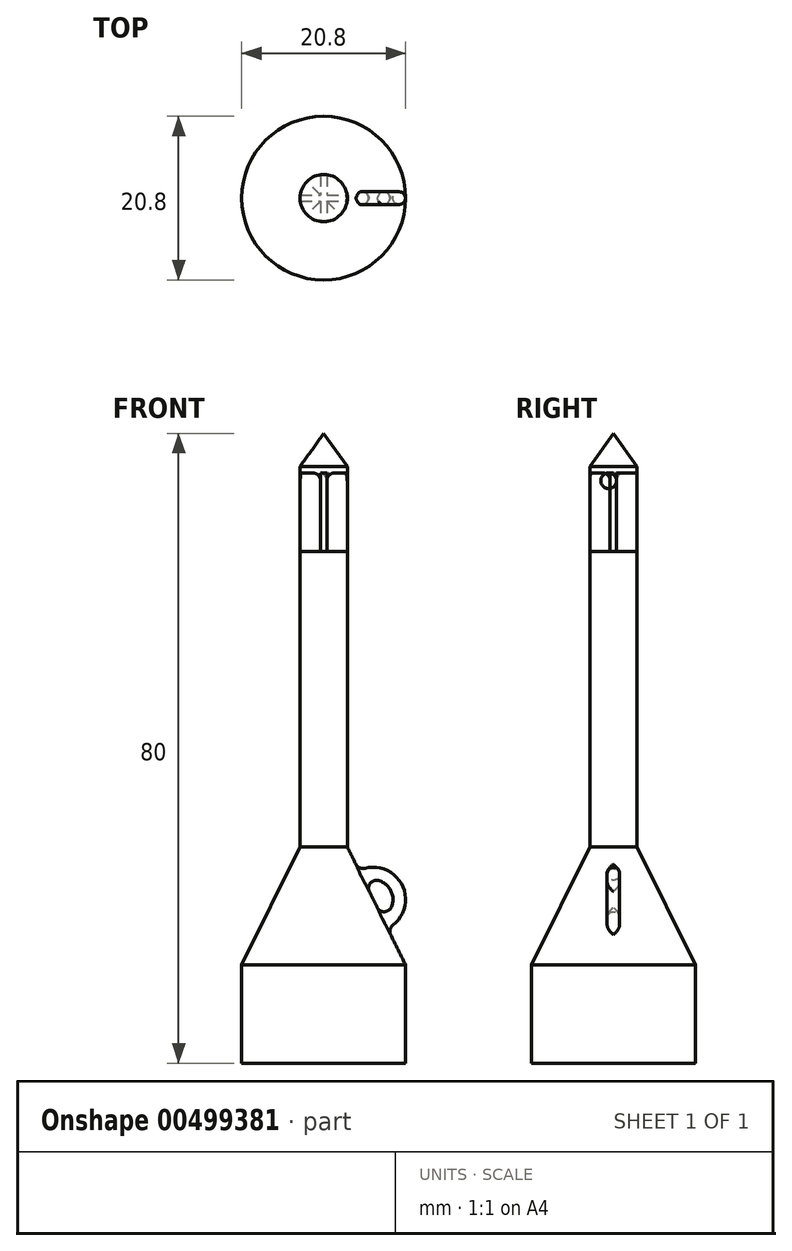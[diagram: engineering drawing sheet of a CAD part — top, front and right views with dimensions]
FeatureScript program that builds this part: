
annotation { "Feature Type Name" : "Feature", "Feature Type Description" : "" }
export const myFeature = defineFeature(function(context is Context, id is Id, definition is map)
    precondition{}
    {
        {
            var Q0;
            Q0=qCreatedBy(makeId("Front.planeOp"),FACE);
            var sketch = newSketch(context, id + "F0", { "sketchPlane" : qUnion([Q0])});
            skLineSegment(sketch, "E0", {"start": v(0, 0) * mm, "end": v(10.4, 0) * mm});
            skLineSegment(sketch, "E1", {"start": v(10.4, 0) * mm, "end": v(10.4, 12.5) * mm});
            skLineSegment(sketch, "E2", {"start": v(10.4, 12.5) * mm, "end": v(3, 27.5) * mm});
            skLineSegment(sketch, "E3", {"start": v(3, 27.5) * mm, "end": v(3, 65) * mm});
            skLineSegment(sketch, "E4", {"start": v(3, 65) * mm, "end": v(0, 65) * mm});
            skLineSegment(sketch, "E5", {"start": v(0, 65) * mm, "end": v(0, 0) * mm});
            skLineSegment(sketch, "E6", {"start": v(0, 53.14) * mm, "end": v(0, -5.64) * mm, "construction": true});
            skSolve(sketch);
        }
        {
            var Q0;
            Q0=makeQuery(id+"F0.imprint","IMPRINT",FACE,{"disambiguationData":[TD([[makeQuery(id+"F0.imprint","IMPRINT",EDGE,{"derivedFrom":sQuery(id+"F0.wireOp",EDGE,"E0")}),1.0]])]});
            var Q1;
            Q1=qConstructionFilter(qBodyType(qCreatedBy(id+"F0",EDGE),BodyType.WIRE),ConstructionObject.NO);
            var Q2;
            Q2=sQuery(id+"F0.wireOp",EDGE,"E6");
            revolve(context, id + "F1", {"entities" : qUnion([Q0]), "surfaceEntities" : qUnion([Q1]), "axis" : qUnion([Q2]), "revolveType" : RevolveType.FULL});
        }
        {
            var Q0;
            Q0=qCreatedBy(makeId("Front.planeOp"),FACE);
            var sketch = newSketch(context, id + "F2", { "sketchPlane" : qUnion([Q0])});
            skArc(sketch, "E7", {"start": v(6.96, 16.75) * mm, "mid": v(9.98, 22.61) * mm, "end": v(3.5, 23.79) * mm});
            skArc(sketch, "E8", {"start": v(6.2, 18.3) * mm, "mid": v(8.54, 21.9) * mm, "end": v(4.26, 22.24) * mm});
            skLineSegment(sketch, "E9", {"start": v(-9.82, 13.68) * mm, "end": v(-0.94, 31.69) * mm, "construction": true});
            skLineSegment(sketch, "E10", {"start": v(0.94, 31.69) * mm, "end": v(9.82, 13.68) * mm, "construction": true});
            skLineSegment(sketch, "E11", {"start": v(3.5, 23.79) * mm, "end": v(4.26, 22.24) * mm});
            skLineSegment(sketch, "E12.trimOffspring", {"start": v(6.2, 18.3) * mm, "end": v(6.96, 16.75) * mm});
            skLineSegment(sketch, "E13", {"start": v(0, 43.75) * mm, "end": v(0, 5.8) * mm, "construction": true});
            skArc(sketch, "E14.MirrorCS", {"start": v(-6.96, 16.75) * mm, "mid": v(-9.98, 22.61) * mm, "end": v(-3.5, 23.79) * mm});
            skArc(sketch, "E15.MirrorCS", {"start": v(-6.2, 18.3) * mm, "mid": v(-8.54, 21.9) * mm, "end": v(-4.26, 22.24) * mm});
            skLineSegment(sketch, "E16.MirrorCS", {"start": v(-6.2, 18.3) * mm, "end": v(-6.96, 16.75) * mm});
            skLineSegment(sketch, "E17.MirrorCS", {"start": v(-3.5, 23.79) * mm, "end": v(-4.26, 22.24) * mm});
            skSolve(sketch);
        }
        {
            var Q0;
            Q0=makeQuery(id+"F2.imprint","IMPRINT",FACE,{"disambiguationData":[TD([[makeQuery(id+"F2.imprint","IMPRINT",EDGE,{"derivedFrom":sQuery(id+"F2.wireOp",EDGE,"E14.MirrorCS")}),-1.0]])]});
            var Q1;
            Q1=makeQuery(id+"F2.imprint","IMPRINT",FACE,{"disambiguationData":[TD([[makeQuery(id+"F2.imprint","IMPRINT",EDGE,{"derivedFrom":sQuery(id+"F2.wireOp",EDGE,"E7")}),1.0]])]});
            extrude(context, id + "F3", {"entities" : qUnion([Q0, Q1]), "operationType" : NewBodyOperationType.ADD, "endBound" : BoundingType.SYMMETRIC, "depth" : 1.6 * mm});
        }
        {
            var Q0;
            Q0=makeQuery(id+"F1.opRevolve","SWEPT_FACE",FACE,{"disambiguationData":[OSD([sQuery(id+"F0.wireOp",EDGE,"E4")])]});
            var sketch = newSketch(context, id + "F4", { "sketchPlane" : qUnion([Q0])});
            skLineSegment(sketch, "E18.bottom", {"start": v(-0.4, 3) * mm, "end": v(0.4, 3) * mm});
            skLineSegment(sketch, "E18.top", {"start": v(-0.4, -3) * mm, "end": v(0.4, -3) * mm});
            skLineSegment(sketch, "E18.left", {"start": v(-0.4, 3) * mm, "end": v(-0.4, 0.4) * mm});
            skLineSegment(sketch, "E18.right", {"start": v(0.4, 3) * mm, "end": v(0.4, 0.4) * mm});
            skLineSegment(sketch, "E19.bottom", {"start": v(-3, 0.4) * mm, "end": v(-0.4, 0.4) * mm});
            skLineSegment(sketch, "E19.top", {"start": v(-3, -0.4) * mm, "end": v(-0.4, -0.4) * mm});
            skLineSegment(sketch, "E19.left", {"start": v(-3, 0.4) * mm, "end": v(-3, -0.4) * mm});
            skLineSegment(sketch, "E19.right", {"start": v(3, 0.4) * mm, "end": v(3, -0.4) * mm});
            skLineSegment(sketch, "E20", {"start": v(0, 2.58) * mm, "end": v(0, -2.8) * mm, "construction": true});
            skLineSegment(sketch, "E21", {"start": v(-2.51, 0) * mm, "end": v(2.57, 0) * mm, "construction": true});
            skLineSegment(sketch, "E22.trimOffspring", {"start": v(0.4, 0.4) * mm, "end": v(3, 0.4) * mm});
            skLineSegment(sketch, "E23.trimOffspring", {"start": v(0.4, -0.4) * mm, "end": v(0.4, -3) * mm});
            skLineSegment(sketch, "E24.trimOffspring", {"start": v(0.4, -0.4) * mm, "end": v(3, -0.4) * mm});
            skLineSegment(sketch, "E25.trimOffspring", {"start": v(-0.4, -0.4) * mm, "end": v(-0.4, -3) * mm});
            skSolve(sketch);
        }
        {
            var Q0;
            Q0=qSketchRegion(id+"F4",true);
            extrude(context, id + "F5", {"entities" : qUnion([Q0]), "operationType" : NewBodyOperationType.ADD, "depth" : 10 * mm});
        }
        {
            var Q0;
            Q0=qCreatedBy(makeId("Front.planeOp"),FACE);
            var sketch = newSketch(context, id + "F6", { "sketchPlane" : qUnion([Q0])});
            skLineSegment(sketch, "E26.0.0", {"start": v(0.4, 65) * mm, "end": v(2.97, 65) * mm, "construction": true});
            skLineSegment(sketch, "E26.0.1", {"start": v(2.97, 65) * mm, "end": v(3, 65) * mm, "construction": true});
            skLineSegment(sketch, "E26.0.2", {"start": v(3, 65) * mm, "end": v(3, 75) * mm, "construction": true});
            skLineSegment(sketch, "E26.0.4", {"start": v(0.4, 75) * mm, "end": v(0.4, 65) * mm, "construction": true});
            skLineSegment(sketch, "E27", {"start": v(0, 83.64) * mm, "end": v(0, 72.25) * mm, "construction": true});
            skLineSegment(sketch, "E28", {"start": v(3, 75) * mm, "end": v(3, 75.8) * mm});
            skLineSegment(sketch, "E29", {"start": v(3, 75.8) * mm, "end": v(0, 80) * mm});
            skLineSegment(sketch, "E30", {"start": v(0, 80) * mm, "end": v(0, 75) * mm});
            skLineSegment(sketch, "E31", {"start": v(0, 75) * mm, "end": v(3, 75) * mm});
            skSolve(sketch);
        }
        {
            var Q0;
            Q0=makeQuery(id+"F6.imprint","IMPRINT",FACE,{"disambiguationData":[TD([[makeQuery(id+"F6.imprint","IMPRINT",EDGE,{"derivedFrom":sQuery(id+"F6.wireOp",EDGE,"sfQvweTP-yfMo-TDxM-7ycy-mknhdcVdmoTF")}),1.0]])]});
            var Q1;
            Q1=makeQuery(id+"F6.imprint","IMPRINT",FACE,{"disambiguationData":[TD([[makeQuery(id+"F6.imprint","IMPRINT",EDGE,{"derivedFrom":sQuery(id+"F6.wireOp",EDGE,"E28")}),1.0]])]});
            var Q2;
            Q2=sQuery(id+"F6.wireOp",EDGE,"E27");
            revolve(context, id + "F7", {"operationType" : NewBodyOperationType.ADD, "entities" : qUnion([Q0, Q1]), "axis" : qUnion([Q2]), "revolveType" : RevolveType.FULL});
        }
        {
            var Q0;
            Q0=makeQuery(id+"F3.boolean.opBoolean","INTERSECT",EDGE,{"disambiguationData":[OD(0.0)],"derivedFrom":[makeQuery(id+"F1.opRevolve","SWEPT_FACE",FACE,{"disambiguationData":[OSD([sQuery(id+"F0.wireOp",EDGE,"E2")])]}),makeQuery(id+"F3.opExtrude","SWEPT_FACE",FACE,{"disambiguationData":[OSD([sQuery(id+"F2.wireOp",EDGE,"E7")])]})]});
            var Q1;
            Q1=makeQuery(id+"F3.boolean.opBoolean","INTERSECT",EDGE,{"disambiguationData":[OD(1.0)],"derivedFrom":[makeQuery(id+"F1.opRevolve","SWEPT_FACE",FACE,{"disambiguationData":[OSD([sQuery(id+"F0.wireOp",EDGE,"E2")])]}),makeQuery(id+"F3.opExtrude","SWEPT_FACE",FACE,{"disambiguationData":[OSD([sQuery(id+"F2.wireOp",EDGE,"E14.MirrorCS")])]})]});
            var Q2;
            Q2=makeQuery(id+"F3.boolean.opBoolean","INTERSECT",EDGE,{"disambiguationData":[OD(0.0)],"derivedFrom":[makeQuery(id+"F1.opRevolve","SWEPT_FACE",FACE,{"disambiguationData":[OSD([sQuery(id+"F0.wireOp",EDGE,"E2")])]}),makeQuery(id+"F3.opExtrude","SWEPT_FACE",FACE,{"disambiguationData":[OSD([sQuery(id+"F2.wireOp",EDGE,"E15.MirrorCS")])]})]});
            var Q3;
            Q3=makeQuery(id+"F3.boolean.opBoolean","INTERSECT",EDGE,{"disambiguationData":[OD(1.0)],"derivedFrom":[makeQuery(id+"F1.opRevolve","SWEPT_FACE",FACE,{"disambiguationData":[OSD([sQuery(id+"F0.wireOp",EDGE,"E2")])]}),makeQuery(id+"F3.opExtrude","SWEPT_FACE",FACE,{"disambiguationData":[OSD([sQuery(id+"F2.wireOp",EDGE,"E8")])]})]});
            var Q4;
            Q4=makeQuery(id+"F3.boolean.opBoolean","INTERSECT",EDGE,{"disambiguationData":[OD(1.0)],"derivedFrom":[makeQuery(id+"F1.opRevolve","SWEPT_FACE",FACE,{"disambiguationData":[OSD([sQuery(id+"F0.wireOp",EDGE,"E2")])]}),makeQuery(id+"F3.opExtrude","SWEPT_FACE",FACE,{"disambiguationData":[OSD([sQuery(id+"F2.wireOp",EDGE,"E7")])]})]});
            var Q5;
            Q5=makeQuery(id+"F3.boolean.opBoolean","INTERSECT",EDGE,{"disambiguationData":[OD(0.0)],"derivedFrom":[makeQuery(id+"F1.opRevolve","SWEPT_FACE",FACE,{"disambiguationData":[OSD([sQuery(id+"F0.wireOp",EDGE,"E2")])]}),makeQuery(id+"F3.opExtrude","SWEPT_FACE",FACE,{"disambiguationData":[OSD([sQuery(id+"F2.wireOp",EDGE,"E14.MirrorCS")])]})]});
            var Q6;
            Q6=makeQuery(id+"F3.boolean.opBoolean","INTERSECT",EDGE,{"disambiguationData":[OD(1.0)],"derivedFrom":[makeQuery(id+"F1.opRevolve","SWEPT_FACE",FACE,{"disambiguationData":[OSD([sQuery(id+"F0.wireOp",EDGE,"E2")])]}),makeQuery(id+"F3.opExtrude","SWEPT_FACE",FACE,{"disambiguationData":[OSD([sQuery(id+"F2.wireOp",EDGE,"E15.MirrorCS")])]})]});
            var Q7;
            Q7=makeQuery(id+"F3.boolean.opBoolean","INTERSECT",EDGE,{"disambiguationData":[OD(0.0)],"derivedFrom":[makeQuery(id+"F1.opRevolve","SWEPT_FACE",FACE,{"disambiguationData":[OSD([sQuery(id+"F0.wireOp",EDGE,"E2")])]}),makeQuery(id+"F3.opExtrude","SWEPT_FACE",FACE,{"disambiguationData":[OSD([sQuery(id+"F2.wireOp",EDGE,"E8")])]})]});
            fillet(context, id + "F8", {"entities" : qUnion([Q0, Q1, Q2, Q3, Q4, Q5, Q6, Q7]), "radius" : 1 * mm, "tangentPropagation" : true, "allowEdgeOverflow" : false});
        }
        {
            var Q0;
            {var subQ0=sQuery(id+"F4.wireOp",EDGE,"E19.top");Q0=makeQuery(id+"F7.boolean.opBoolean","SPLIT",EDGE,{"disambiguationData":[topologyDisambiguationEdgeConnected([makeQuery(id+"F7.opRevolve","SWEPT_FACE",FACE,{"disambiguationData":[OSD([sQuery(id+"F6.wireOp",EDGE,"E31")])]})])],"derivedFrom":makeQuery(id+"F5.opExtrude","CAP_EDGE",EDGE,{"disambiguationData":[OSD([subQ0])],"isStart":false})});}
            var Q1;
            {var subQ0=sQuery(id+"F4.wireOp",EDGE,"E24.trimOffspring");Q1=makeQuery(id+"F7.boolean.opBoolean","SPLIT",EDGE,{"disambiguationData":[topologyDisambiguationEdgeConnected([makeQuery(id+"F7.opRevolve","SWEPT_FACE",FACE,{"disambiguationData":[OSD([sQuery(id+"F6.wireOp",EDGE,"E31")])]})])],"derivedFrom":makeQuery(id+"F5.opExtrude","CAP_EDGE",EDGE,{"disambiguationData":[OSD([subQ0])],"isStart":false})});}
            var Q2;
            {var subQ0=sQuery(id+"F4.wireOp",EDGE,"E25.trimOffspring");Q2=makeQuery(id+"F7.boolean.opBoolean","SPLIT",EDGE,{"disambiguationData":[topologyDisambiguationEdgeConnected([makeQuery(id+"F7.opRevolve","SWEPT_FACE",FACE,{"disambiguationData":[OSD([sQuery(id+"F6.wireOp",EDGE,"E31")])]})])],"derivedFrom":makeQuery(id+"F5.opExtrude","CAP_EDGE",EDGE,{"disambiguationData":[OSD([subQ0])],"isStart":false})});}
            var Q3;
            {var subQ0=sQuery(id+"F4.wireOp",EDGE,"E22.trimOffspring");Q3=makeQuery(id+"F7.boolean.opBoolean","SPLIT",EDGE,{"disambiguationData":[topologyDisambiguationEdgeConnected([makeQuery(id+"F7.opRevolve","SWEPT_FACE",FACE,{"disambiguationData":[OSD([sQuery(id+"F6.wireOp",EDGE,"E31")])]})])],"derivedFrom":makeQuery(id+"F5.opExtrude","CAP_EDGE",EDGE,{"disambiguationData":[OSD([subQ0])],"isStart":false})});}
            var Q4;
            {var subQ0=sQuery(id+"F4.wireOp",EDGE,"E19.bottom");Q4=makeQuery(id+"F7.boolean.opBoolean","SPLIT",EDGE,{"disambiguationData":[topologyDisambiguationEdgeConnected([makeQuery(id+"F7.opRevolve","SWEPT_FACE",FACE,{"disambiguationData":[OSD([sQuery(id+"F6.wireOp",EDGE,"E31")])]})])],"derivedFrom":makeQuery(id+"F5.opExtrude","CAP_EDGE",EDGE,{"disambiguationData":[OSD([subQ0])],"isStart":false})});}
            var Q5;
            {var subQ0=sQuery(id+"F4.wireOp",EDGE,"E18.right");Q5=makeQuery(id+"F7.boolean.opBoolean","SPLIT",EDGE,{"disambiguationData":[topologyDisambiguationEdgeConnected([makeQuery(id+"F7.opRevolve","SWEPT_FACE",FACE,{"disambiguationData":[OSD([sQuery(id+"F6.wireOp",EDGE,"E31")])]})])],"derivedFrom":makeQuery(id+"F5.opExtrude","CAP_EDGE",EDGE,{"disambiguationData":[OSD([subQ0])],"isStart":false})});}
            var Q6;
            {var subQ0=sQuery(id+"F4.wireOp",EDGE,"E23.trimOffspring");Q6=makeQuery(id+"F7.boolean.opBoolean","SPLIT",EDGE,{"disambiguationData":[topologyDisambiguationEdgeConnected([makeQuery(id+"F7.opRevolve","SWEPT_FACE",FACE,{"disambiguationData":[OSD([sQuery(id+"F6.wireOp",EDGE,"E31")])]})])],"derivedFrom":makeQuery(id+"F5.opExtrude","CAP_EDGE",EDGE,{"disambiguationData":[OSD([subQ0])],"isStart":false})});}
            var Q7;
            {var subQ0=sQuery(id+"F4.wireOp",EDGE,"E18.left");Q7=makeQuery(id+"F7.boolean.opBoolean","SPLIT",EDGE,{"disambiguationData":[topologyDisambiguationEdgeConnected([makeQuery(id+"F7.opRevolve","SWEPT_FACE",FACE,{"disambiguationData":[OSD([sQuery(id+"F6.wireOp",EDGE,"E31")])]})])],"derivedFrom":makeQuery(id+"F5.opExtrude","CAP_EDGE",EDGE,{"disambiguationData":[OSD([subQ0])],"isStart":false})});}
            fillet(context, id + "F9", {"entities" : qUnion([Q0, Q1, Q2, Q3, Q4, Q5, Q6, Q7]), "radius" : 1 * mm, "tangentPropagation" : true, "allowEdgeOverflow" : false});
        }
        {
            var Q0;
            Q0=makeQuery(id+"F3.opExtrude","CAP_EDGE",EDGE,{"disambiguationData":[OSD([sQuery(id+"F2.wireOp",EDGE,"E14.MirrorCS")])],"isStart":true});
            var Q1;
            Q1=makeQuery(id+"F3.opExtrude","CAP_EDGE",EDGE,{"disambiguationData":[OSD([sQuery(id+"F2.wireOp",EDGE,"E14.MirrorCS")])],"isStart":false});
            var Q2;
            Q2=makeQuery(id+"F3.opExtrude","CAP_EDGE",EDGE,{"disambiguationData":[OSD([sQuery(id+"F2.wireOp",EDGE,"E15.MirrorCS")])],"isStart":true});
            var Q3;
            Q3=makeQuery(id+"F3.opExtrude","CAP_EDGE",EDGE,{"disambiguationData":[OSD([sQuery(id+"F2.wireOp",EDGE,"E15.MirrorCS")])],"isStart":false});
            var Q4;
            Q4=makeQuery(id+"F3.opExtrude","CAP_EDGE",EDGE,{"disambiguationData":[OSD([sQuery(id+"F2.wireOp",EDGE,"E8")])],"isStart":false});
            var Q5;
            Q5=makeQuery(id+"F3.opExtrude","CAP_EDGE",EDGE,{"disambiguationData":[OSD([sQuery(id+"F2.wireOp",EDGE,"E7")])],"isStart":false});
            var Q6;
            {var subQ0=sQuery(id+"F2.wireOp",EDGE,"E8");Q6=makeQuery(id+"F8.opFillet","BLEND_EDGE",EDGE,{"blendedFrom":[makeQuery(id+"F3.boolean.opBoolean","INTERSECT",EDGE,{"disambiguationData":[OD(0.0)],"derivedFrom":[makeQuery(id+"F1.opRevolve","SWEPT_FACE",FACE,{"disambiguationData":[OSD([sQuery(id+"F0.wireOp",EDGE,"E2")])]}),makeQuery(id+"F3.opExtrude","SWEPT_FACE",FACE,{"disambiguationData":[OSD([subQ0])]})]}),makeQuery(id+"F3.opExtrude","CAP_FACE",FACE,{"disambiguationData":[OSD([sQuery(id+"F2.wireOp",EDGE,"E7"),subQ0,sQuery(id+"F2.wireOp",EDGE,"E11"),sQuery(id+"F2.wireOp",EDGE,"E12.trimOffspring")])],"isStart":true})],"blendedInto":[makeQuery(id+"F3.opExtrude","CAP_FACE",FACE,{"disambiguationData":[OSD([sQuery(id+"F2.wireOp",EDGE,"E7"),subQ0,sQuery(id+"F2.wireOp",EDGE,"E11"),sQuery(id+"F2.wireOp",EDGE,"E12.trimOffspring")])],"isStart":true})]});}
            var Q7;
            Q7=makeQuery(id+"F3.opExtrude","CAP_EDGE",EDGE,{"disambiguationData":[OSD([sQuery(id+"F2.wireOp",EDGE,"E7")])],"isStart":true});
            fillet(context, id + "F10", {"entities" : qUnion([Q0, Q1, Q2, Q3, Q4, Q5, Q6, Q7]), "radius" : 0.8 * mm, "tangentPropagation" : true, "allowEdgeOverflow" : false});
        }
    });
